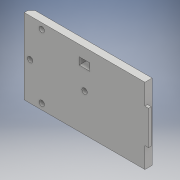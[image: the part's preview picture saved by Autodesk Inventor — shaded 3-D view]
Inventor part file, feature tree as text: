
AUTODESK INVENTOR PART (.ipt)
format: ipt  version: 2017 (Build 210142000, 142)  size: 326,656 bytes
history: native  units: mm
features: sketch x6, extrude x4, projected_geometry x4, hole x1, chamfer x1
ambient origin geometry x8: Origin, YZ Plane, XZ Plane, XY Plane, X Axis, Y Axis, Z Axis, Center Point
bodies: Solid1 (feature_tree)
feature tree (16):
  extrude  "Extrusion1"  Depth=10.0mm
  extrude  "Extrusion2"  Depth=2.0mm TaperAngle=0.0deg
  sketch  "Sketch3"  dims[d10=3.0mm d11=6.0mm d12=4.0mm d13=2.0mm d14=90.0deg d15=8.0mm d16=20.594885mm d20=0.5mm]
  hole  "Hole1"  [1 undecoded]
  extrude  "Extrusion4"  Depth=0.5mm
  extrude  "Extrusion5"  Depth=10.0mm
  chamfer  "Chamfer1"  Distance=6.0mm
  sketch  "Sketch1"  dims[d0=6.5mm d1=6.5mm d2=6.5mm d3=6.5mm d4=10.0mm d5=10.0mm]
  sketch  "Sketch2"  dims[d6=2.0mm d7=0.0mm d8=2.0mm d9=0.0mm]
  projected_geometry  "Projected Loop1"
  sketch  "Sketch4"  dims[d21=0.5mm d22=0.5mm]
  projected_geometry  "Projected Loop2"
  sketch  "Sketch5"  dims[d23=2.0mm d24=0.0mm d25=10.0mm d26=10.0mm]
  projected_geometry  "Projected Loop3"
  sketch  "Sketch6"  dims[d27=4.0mm d28=6.0mm d29=6.0mm d30=10.0mm d31=0.0mm d32=2.0mm d33=2.0mm d34=45.0deg]
  projected_geometry  "Projected Loop4"
note: 1 required parameter value undecoded (feature->parameter linkage not recoverable at this tier; creation-order binding heuristic only, values carry confidence <= 0.55)
